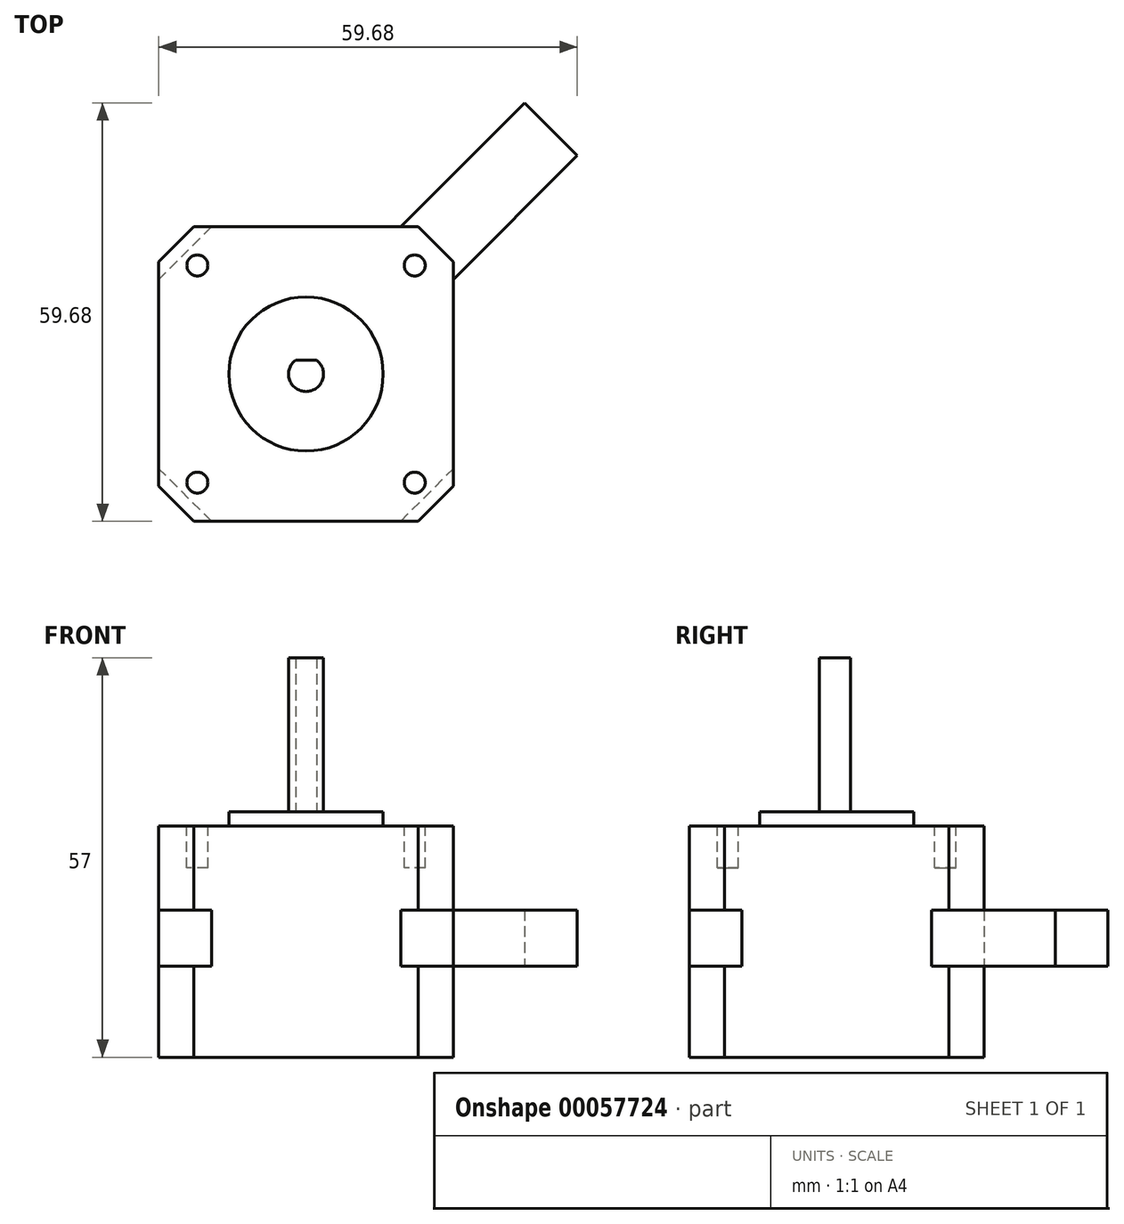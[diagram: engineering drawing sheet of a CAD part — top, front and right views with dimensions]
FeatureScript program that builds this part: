
annotation { "Feature Type Name" : "Feature", "Feature Type Description" : "" }
export const myFeature = defineFeature(function(context is Context, id is Id, definition is map)
    precondition{}
    {
        {
            var Q0;
            Q0=qCreatedBy(makeId("Top.planeOp"),FACE);
            var sketch = newSketch(context, id + "F0", { "sketchPlane" : qUnion([Q0])});
            skLineSegment(sketch, "E0.bottom", {"start": v(-21, 21) * mm, "end": v(21, 21) * mm});
            skLineSegment(sketch, "E0.top", {"start": v(-21, -21) * mm, "end": v(21, -21) * mm});
            skLineSegment(sketch, "E0.left", {"start": v(-21, 21) * mm, "end": v(-21, -21) * mm});
            skLineSegment(sketch, "E0.right", {"start": v(21, 21) * mm, "end": v(21, -21) * mm});
            skSolve(sketch);
        }
        {
            var Q0;
            Q0=makeQuery(id+"F0.imprint","IMPRINT",FACE,{"disambiguationData":[TD([[makeQuery(id+"F0.imprint","IMPRINT",EDGE,{"derivedFrom":sQuery(id+"F0.wireOp",EDGE,"E0.bottom")}),-1.0]])]});
            extrude(context, id + "F1", {"entities" : qUnion([Q0]), "endBound" : BoundingType.SYMMETRIC, "depth" : 8 * mm});
        }
        {
            var Q0;
            Q0=makeQuery(id+"F1.opExtrude","SWEPT_EDGE",EDGE,{"disambiguationData":[OSD([sQuery(id+"F0.wireOp",EDGE,"E0.bottom"),sQuery(id+"F0.wireOp",EDGE,"E0.right")])]});
            var Q1;
            Q1=makeQuery(id+"F1.opExtrude","SWEPT_EDGE",EDGE,{"disambiguationData":[OSD([sQuery(id+"F0.wireOp",EDGE,"E0.bottom"),sQuery(id+"F0.wireOp",EDGE,"E0.left")])]});
            var Q2;
            Q2=makeQuery(id+"F1.opExtrude","SWEPT_EDGE",EDGE,{"disambiguationData":[OSD([sQuery(id+"F0.wireOp",EDGE,"E0.top"),sQuery(id+"F0.wireOp",EDGE,"E0.left")])]});
            var Q3;
            Q3=makeQuery(id+"F1.opExtrude","SWEPT_EDGE",EDGE,{"disambiguationData":[OSD([sQuery(id+"F0.wireOp",EDGE,"E0.top"),sQuery(id+"F0.wireOp",EDGE,"E0.right")])]});
            chamfer(context, id + "F2", {"entities" : qUnion([Q0, Q1, Q2, Q3]), "width" : 7.5 * mm, "tangentPropagation" : true});
        }
        {
            var Q0;
            Q0=makeQuery(id+"F1.opExtrude","CAP_FACE",FACE,{"disambiguationData":[OSD([sQuery(id+"F0.wireOp",EDGE,"E0.bottom"),sQuery(id+"F0.wireOp",EDGE,"E0.top"),sQuery(id+"F0.wireOp",EDGE,"E0.left"),sQuery(id+"F0.wireOp",EDGE,"E0.right")])],"isStart":false});
            var sketch = newSketch(context, id + "F3", { "sketchPlane" : qUnion([Q0])});
            skLineSegment(sketch, "E1.0", {"start": v(-21, 21) * mm, "end": v(21, 21) * mm});
            skLineSegment(sketch, "E1.1", {"start": v(-21, 21) * mm, "end": v(-21, -21) * mm});
            skLineSegment(sketch, "E1.2", {"start": v(-21, -21) * mm, "end": v(21, -21) * mm});
            skLineSegment(sketch, "E1.3", {"start": v(21, 21) * mm, "end": v(21, -21) * mm});
            skSolve(sketch);
        }
        {
            var Q0;
            {var subQ0=sQuery(id+"F0.wireOp",EDGE,"E0.top");var subQ1=sQuery(id+"F0.wireOp",EDGE,"E0.right");var subQ2=sQuery(id+"F0.wireOp",EDGE,"E0.bottom");var subQ3=sQuery(id+"F0.wireOp",EDGE,"E0.left");var subQ4=makeQuery(id+"F1.opExtrude","CAP_FACE",FACE,{"disambiguationData":[OSD([subQ2,subQ0,subQ3,subQ1])],"isStart":false});var subQ8=makeQuery(id+"F2.opChamfer","BLEND_EDGE",EDGE,{"blendedFrom":[makeQuery(id+"F1.opExtrude","SWEPT_EDGE",EDGE,{"disambiguationData":[OSD([subQ2,subQ3])]}),subQ4],"blendedInto":[subQ4]});Q0=makeQuery(id+"F3.imprint","IMPRINT",FACE,{"disambiguationData":[TD([[makeQuery(id+"F3.imprint","IMPRINT",EDGE,{"derivedFrom":subQ8}),1.0]])]});}
            var Q1;
            {var subQ0=sQuery(id+"F0.wireOp",EDGE,"E0.bottom");var subQ1=sQuery(id+"F0.wireOp",EDGE,"E0.right");var subQ2=makeQuery(id+"F2.opChamfer","BLEND_EDGE",EDGE,{"blendedFrom":[makeQuery(id+"F1.opExtrude","SWEPT_EDGE",EDGE,{"disambiguationData":[OSD([subQ0,subQ1])]}),makeQuery(id+"F1.opExtrude","CAP_FACE",FACE,{"disambiguationData":[OSD([subQ0,sQuery(id+"F0.wireOp",EDGE,"E0.top"),sQuery(id+"F0.wireOp",EDGE,"E0.left"),subQ1])],"isStart":false})],"blendedInto":[makeQuery(id+"F1.opExtrude","CAP_FACE",FACE,{"disambiguationData":[OSD([subQ0,sQuery(id+"F0.wireOp",EDGE,"E0.top"),sQuery(id+"F0.wireOp",EDGE,"E0.left"),subQ1])],"isStart":false})]});Q1=makeQuery(id+"F3.imprint","IMPRINT",FACE,{"disambiguationData":[TD([[makeQuery(id+"F3.imprint","IMPRINT",EDGE,{"derivedFrom":subQ2}),-1.0]])]});}
            var Q2;
            {var subQ0=sQuery(id+"F0.wireOp",EDGE,"E0.bottom");var subQ1=sQuery(id+"F0.wireOp",EDGE,"E0.left");var subQ2=makeQuery(id+"F2.opChamfer","BLEND_EDGE",EDGE,{"blendedFrom":[makeQuery(id+"F1.opExtrude","SWEPT_EDGE",EDGE,{"disambiguationData":[OSD([subQ0,subQ1])]}),makeQuery(id+"F1.opExtrude","CAP_FACE",FACE,{"disambiguationData":[OSD([subQ0,sQuery(id+"F0.wireOp",EDGE,"E0.top"),subQ1,sQuery(id+"F0.wireOp",EDGE,"E0.right")])],"isStart":false})],"blendedInto":[makeQuery(id+"F1.opExtrude","CAP_FACE",FACE,{"disambiguationData":[OSD([subQ0,sQuery(id+"F0.wireOp",EDGE,"E0.top"),subQ1,sQuery(id+"F0.wireOp",EDGE,"E0.right")])],"isStart":false})]});Q2=makeQuery(id+"F3.imprint","IMPRINT",FACE,{"disambiguationData":[TD([[makeQuery(id+"F3.imprint","IMPRINT",EDGE,{"derivedFrom":subQ2}),-1.0]])]});}
            var Q3;
            {var subQ0=sQuery(id+"F0.wireOp",EDGE,"E0.top");var subQ1=sQuery(id+"F0.wireOp",EDGE,"E0.left");var subQ2=makeQuery(id+"F2.opChamfer","BLEND_EDGE",EDGE,{"blendedFrom":[makeQuery(id+"F1.opExtrude","SWEPT_EDGE",EDGE,{"disambiguationData":[OSD([subQ0,subQ1])]}),makeQuery(id+"F1.opExtrude","CAP_FACE",FACE,{"disambiguationData":[OSD([sQuery(id+"F0.wireOp",EDGE,"E0.bottom"),subQ0,subQ1,sQuery(id+"F0.wireOp",EDGE,"E0.right")])],"isStart":false})],"blendedInto":[makeQuery(id+"F1.opExtrude","CAP_FACE",FACE,{"disambiguationData":[OSD([sQuery(id+"F0.wireOp",EDGE,"E0.bottom"),subQ0,subQ1,sQuery(id+"F0.wireOp",EDGE,"E0.right")])],"isStart":false})]});Q3=makeQuery(id+"F3.imprint","IMPRINT",FACE,{"disambiguationData":[TD([[makeQuery(id+"F3.imprint","IMPRINT",EDGE,{"derivedFrom":subQ2}),-1.0]])]});}
            var Q4;
            {var subQ0=sQuery(id+"F0.wireOp",EDGE,"E0.top");var subQ1=sQuery(id+"F0.wireOp",EDGE,"E0.right");var subQ2=makeQuery(id+"F2.opChamfer","BLEND_EDGE",EDGE,{"blendedFrom":[makeQuery(id+"F1.opExtrude","SWEPT_EDGE",EDGE,{"disambiguationData":[OSD([subQ0,subQ1])]}),makeQuery(id+"F1.opExtrude","CAP_FACE",FACE,{"disambiguationData":[OSD([sQuery(id+"F0.wireOp",EDGE,"E0.bottom"),subQ0,sQuery(id+"F0.wireOp",EDGE,"E0.left"),subQ1])],"isStart":false})],"blendedInto":[makeQuery(id+"F1.opExtrude","CAP_FACE",FACE,{"disambiguationData":[OSD([sQuery(id+"F0.wireOp",EDGE,"E0.bottom"),subQ0,sQuery(id+"F0.wireOp",EDGE,"E0.left"),subQ1])],"isStart":false})]});Q4=makeQuery(id+"F3.imprint","IMPRINT",FACE,{"disambiguationData":[TD([[makeQuery(id+"F3.imprint","IMPRINT",EDGE,{"derivedFrom":subQ2}),-1.0]])]});}
            extrude(context, id + "F4", {"entities" : qUnion([Q0, Q1, Q2, Q3, Q4]), "operationType" : NewBodyOperationType.ADD, "depth" : 12 * mm});
        }
        {
            var Q0;
            Q0=makeQuery(id+"F4.opExtrude","SWEPT_EDGE",EDGE,{"disambiguationData":[OSD([sQuery(id+"F3.wireOp",EDGE,"E1.2"),sQuery(id+"F3.wireOp",EDGE,"E1.3")])]});
            var Q1;
            Q1=makeQuery(id+"F4.opExtrude","SWEPT_EDGE",EDGE,{"disambiguationData":[OSD([sQuery(id+"F3.wireOp",EDGE,"E1.1"),sQuery(id+"F3.wireOp",EDGE,"E1.2")])]});
            var Q2;
            Q2=makeQuery(id+"F4.opExtrude","SWEPT_EDGE",EDGE,{"disambiguationData":[OSD([sQuery(id+"F3.wireOp",EDGE,"E1.0"),sQuery(id+"F3.wireOp",EDGE,"E1.1")])]});
            var Q3;
            Q3=makeQuery(id+"F4.opExtrude","SWEPT_EDGE",EDGE,{"disambiguationData":[OSD([sQuery(id+"F3.wireOp",EDGE,"E1.0"),sQuery(id+"F3.wireOp",EDGE,"E1.3")])]});
            chamfer(context, id + "F5", {"entities" : qUnion([Q0, Q1, Q2, Q3]), "width" : 5 * mm, "tangentPropagation" : true});
        }
        {
            var Q0;
            Q0=makeQuery(id+"F1.opExtrude","CAP_FACE",FACE,{"disambiguationData":[OSD([sQuery(id+"F0.wireOp",EDGE,"E0.bottom"),sQuery(id+"F0.wireOp",EDGE,"E0.top"),sQuery(id+"F0.wireOp",EDGE,"E0.left"),sQuery(id+"F0.wireOp",EDGE,"E0.right")])],"isStart":true});
            var sketch = newSketch(context, id + "F6", { "sketchPlane" : qUnion([Q0])});
            skLineSegment(sketch, "E2.0.0", {"start": v(21, 16) * mm, "end": v(21, -16) * mm});
            skLineSegment(sketch, "E2.0.1", {"start": v(21, -16) * mm, "end": v(16, -21) * mm});
            skLineSegment(sketch, "E2.0.2", {"start": v(16, -21) * mm, "end": v(-16, -21) * mm});
            skLineSegment(sketch, "E2.0.3", {"start": v(-16, -21) * mm, "end": v(-21, -16) * mm});
            skLineSegment(sketch, "E2.0.4", {"start": v(-21, -16) * mm, "end": v(-21, 16) * mm});
            skLineSegment(sketch, "E2.0.5", {"start": v(-21, 16) * mm, "end": v(-16, 21) * mm});
            skLineSegment(sketch, "E2.0.6", {"start": v(-16, 21) * mm, "end": v(16, 21) * mm});
            skLineSegment(sketch, "E2.0.7", {"start": v(16, 21) * mm, "end": v(21, 16) * mm});
            skSolve(sketch);
        }
        {
            var Q0;
            Q0=qSketchRegion(id+"F6",true);
            extrude(context, id + "F7", {"entities" : qUnion([Q0]), "operationType" : NewBodyOperationType.ADD, "depth" : 13 * mm});
        }
        {
            var Q0;
            Q0=makeQuery(id+"F4.opExtrude","CAP_FACE",FACE,{"disambiguationData":[OSD([sQuery(id+"F3.wireOp",EDGE,"E1.0"),sQuery(id+"F3.wireOp",EDGE,"E1.1"),sQuery(id+"F3.wireOp",EDGE,"E1.2"),sQuery(id+"F3.wireOp",EDGE,"E1.3")])],"isStart":false});
            var sketch = newSketch(context, id + "F8", { "sketchPlane" : qUnion([Q0])});
            skCircle(sketch, "E3", {"center": v(0, 0) * mm, "radius": 11 * mm});
            skSolve(sketch);
        }
        {
            var Q0;
            Q0=qSketchRegion(id+"F8",true);
            extrude(context, id + "F9", {"entities" : qUnion([Q0]), "operationType" : NewBodyOperationType.ADD, "depth" : 2 * mm});
        }
        {
            var Q0;
            Q0=makeQuery(id+"F9.opExtrude","CAP_FACE",FACE,{"disambiguationData":[OSD([sQuery(id+"F8.wireOp",EDGE,"E3")])],"isStart":false});
            var sketch = newSketch(context, id + "F10", { "sketchPlane" : qUnion([Q0])});
            skCircle(sketch, "E4", {"center": v(0, 0) * mm, "radius": 2.5 * mm});
            skSolve(sketch);
        }
        {
            var Q0;
            Q0=makeQuery(id+"F10.imprint","IMPRINT",FACE,{"disambiguationData":[TD([[makeQuery(id+"F10.imprint","IMPRINT",EDGE,{"derivedFrom":sQuery(id+"F10.wireOp",EDGE,"E4")}),1.0]])]});
            extrude(context, id + "F11", {"entities" : qUnion([Q0]), "operationType" : NewBodyOperationType.ADD, "depth" : 22 * mm});
        }
        {
            var Q0;
            Q0=makeQuery(id+"F11.opExtrude","CAP_FACE",FACE,{"disambiguationData":[OSD([sQuery(id+"F10.wireOp",EDGE,"E4")])],"isStart":false});
            var sketch = newSketch(context, id + "F12", { "sketchPlane" : qUnion([Q0])});
            skLineSegment(sketch, "E5.bottom", {"start": v(-2.63, 2.93) * mm, "end": v(2.62, 2.93) * mm});
            skLineSegment(sketch, "E5.top", {"start": v(-2.63, 2) * mm, "end": v(2.62, 2) * mm});
            skLineSegment(sketch, "E5.left", {"start": v(-2.63, 2.93) * mm, "end": v(-2.63, 2) * mm});
            skLineSegment(sketch, "E5.right", {"start": v(2.62, 2.93) * mm, "end": v(2.62, 2) * mm});
            skSolve(sketch);
        }
        {
            var Q0;
            Q0=qSketchRegion(id+"F12",true);
            extrude(context, id + "F13", {"entities" : qUnion([Q0]), "operationType" : NewBodyOperationType.REMOVE, "oppositeDirection" : true, "depth" : 22 * mm});
        }
        {
            var Q0;
            Q0=makeQuery(id+"F4.opExtrude","CAP_FACE",FACE,{"disambiguationData":[OSD([sQuery(id+"F3.wireOp",EDGE,"E1.0"),sQuery(id+"F3.wireOp",EDGE,"E1.1"),sQuery(id+"F3.wireOp",EDGE,"E1.2"),sQuery(id+"F3.wireOp",EDGE,"E1.3")])],"isStart":false});
            var sketch = newSketch(context, id + "F14", { "sketchPlane" : qUnion([Q0])});
            skCircle(sketch, "E6", {"center": v(-15.5, 15.5) * mm, "radius": 1.5 * mm});
            skCircle(sketch, "E7.MirrorC", {"center": v(15.5, 15.5) * mm, "radius": 1.5 * mm});
            skCircle(sketch, "E8.MirrorC", {"center": v(-15.5, -15.5) * mm, "radius": 1.5 * mm});
            skCircle(sketch, "E9.MirrorC", {"center": v(15.5, -15.5) * mm, "radius": 1.5 * mm});
            skSolve(sketch);
        }
        {
            var Q0;
            Q0=qSketchRegion(id+"F14",true);
            extrude(context, id + "F15", {"entities" : qUnion([Q0]), "operationType" : NewBodyOperationType.REMOVE, "oppositeDirection" : true, "depth" : 6 * mm});
        }
        {
            var Q0;
            Q0=makeQuery(id+"F2.opChamfer","BLEND_FACE",FACE,{"disambiguationData":[OSD([sQuery(id+"F0.wireOp",EDGE,"E0.bottom"),sQuery(id+"F0.wireOp",EDGE,"E0.right")])]});
            extrude(context, id + "F16", {"entities" : qUnion([Q0]), "operationType" : NewBodyOperationType.ADD, "depth" : 25 * mm});
        }
    });
